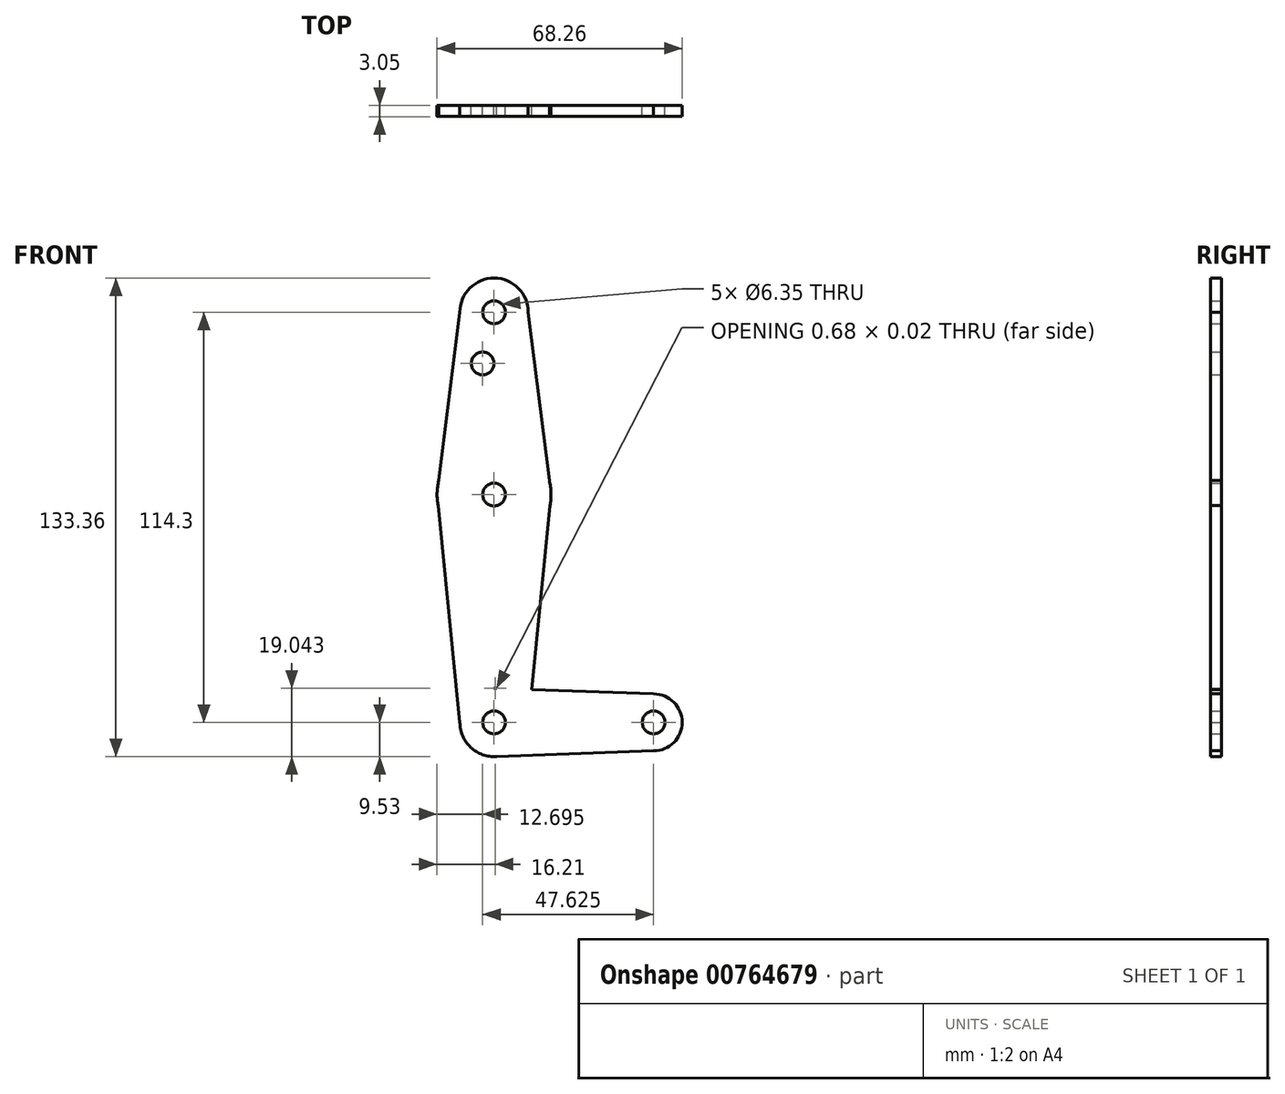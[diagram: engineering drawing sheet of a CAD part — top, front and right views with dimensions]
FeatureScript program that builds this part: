
annotation { "Feature Type Name" : "Feature", "Feature Type Description" : "" }
export const myFeature = defineFeature(function(context is Context, id is Id, definition is map)
    precondition{}
    {
        {
            var Q0;
            Q0=qCreatedBy(makeId("Front.planeOp"),FACE);
            var sketch = newSketch(context, id + "F0", { "sketchPlane" : qUnion([Q0])});
            skLineSegment(sketch, "E0", {"start": v(0, 114.3) * mm, "end": v(0, 0) * mm});
            skLineSegment(sketch, "E1", {"start": v(0, 0) * mm, "end": v(44.45, 0) * mm});
            skCircle(sketch, "E2", {"center": v(0, 0) * mm, "radius": 9.53 * mm});
            skCircle(sketch, "E3", {"center": v(0, 63.5) * mm, "radius": 15.88 * mm});
            skCircle(sketch, "E4", {"center": v(0, 114.3) * mm, "radius": 9.53 * mm});
            skCircle(sketch, "E5", {"center": v(44.45, 0) * mm, "radius": 7.94 * mm});
            skLineSegment(sketch, "E6", {"start": v(-9.52, 114.3) * mm, "end": v(-15.87, 63.5) * mm});
            skLineSegment(sketch, "E7", {"start": v(-15.87, 63.5) * mm, "end": v(-9.57, 0) * mm});
            skLineSegment(sketch, "E8", {"start": v(9.53, 114.3) * mm, "end": v(15.88, 63.5) * mm});
            skLineSegment(sketch, "E9", {"start": v(15.88, 63.5) * mm, "end": v(9.57, 0) * mm});
            skLineSegment(sketch, "E10", {"start": v(0, 9.52) * mm, "end": v(44.45, 7.94) * mm});
            skLineSegment(sketch, "E11", {"start": v(0, -9.53) * mm, "end": v(44.45, -7.94) * mm});
            skLineSegment(sketch, "E12", {"start": v(44.45, -7.94) * mm, "end": v(44.45, 7.94) * mm});
            skLineSegment(sketch, "E13", {"start": v(-9.57, 0) * mm, "end": v(0, 0) * mm});
            skCircle(sketch, "E14", {"center": v(0, 114.3) * mm, "radius": 3.18 * mm});
            skCircle(sketch, "E15", {"center": v(-3.17, 100.03) * mm, "radius": 3.18 * mm});
            skCircle(sketch, "E16", {"center": v(0, 63.5) * mm, "radius": 3.18 * mm});
            skCircle(sketch, "E17", {"center": v(0, 0) * mm, "radius": 3.18 * mm});
            skCircle(sketch, "E18", {"center": v(44.45, 0) * mm, "radius": 3.18 * mm});
            skSolve(sketch);
        }
        {
            var Q0;
            Q0 = qSketchRegion(id + "F0", true);
            var Q1;
            {var subQ5=sQuery(id+"F0.wireOp",EDGE,"E1");var subQ7=sQuery(id+"F0.wireOp",EDGE,"E17");var subQ8=makeQuery(id+"F0.imprint","INTERSECT",VERTEX,{"derivedFrom":[subQ5,subQ7]});Q1=makeQuery(id+"F0.imprint","IMPRINT",FACE,{"disambiguationData":[TD([[makeQuery(id+"F0.imprint","IMPRINT",EDGE,{"disambiguationData":[TD([[subQ8,-1.0]])],"derivedFrom":subQ5}),1.0]])]});}
            extrude(context, id + "F1", {"entities" : qUnion([Q0, Q1]), "depth" : 3.05 * mm, "offsetDistance" : 25.4 * mm});
        }
    });
